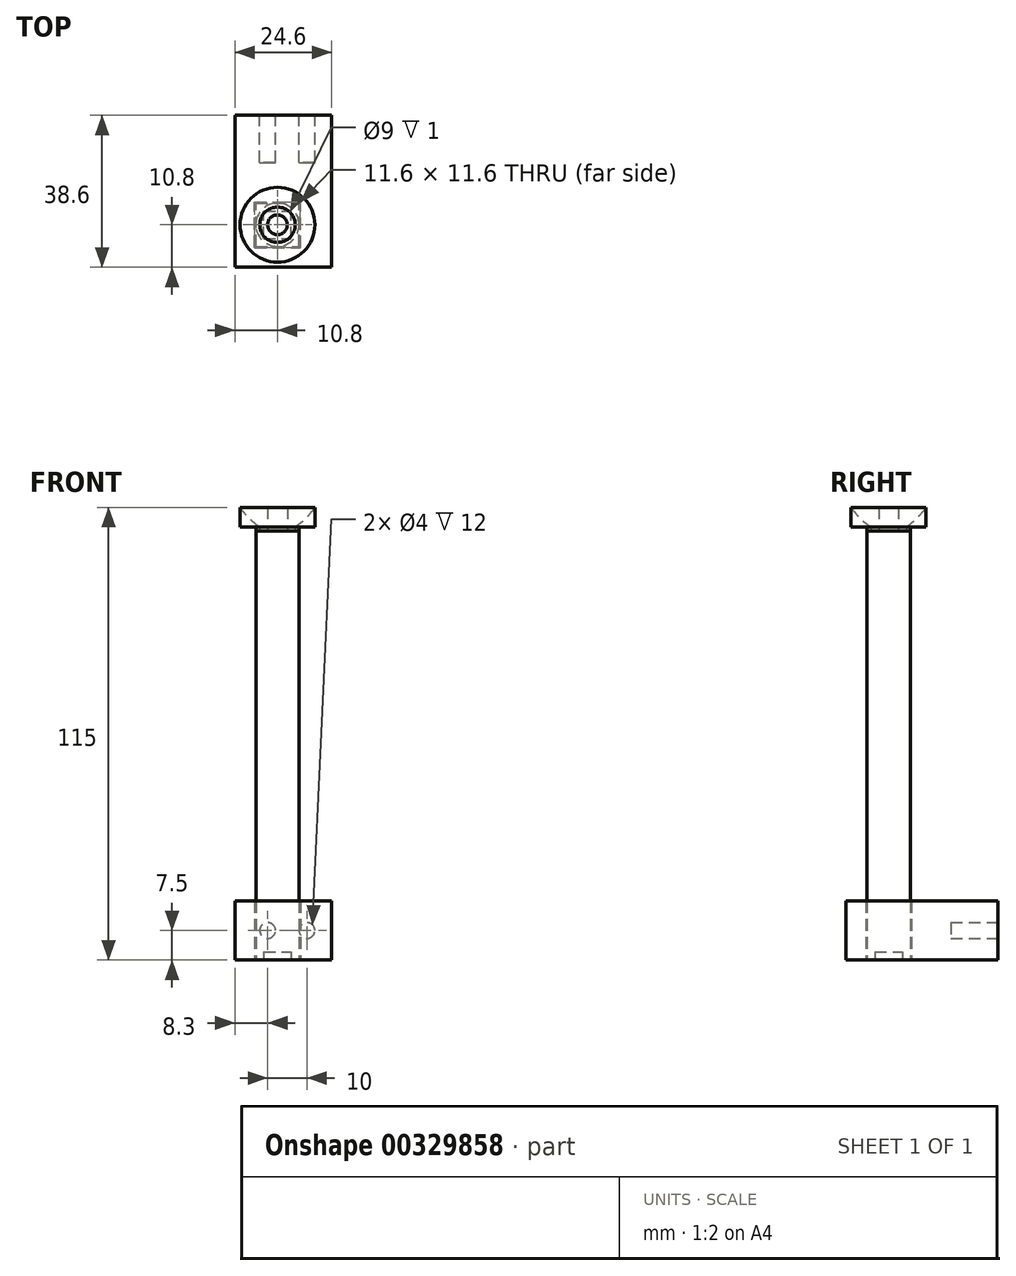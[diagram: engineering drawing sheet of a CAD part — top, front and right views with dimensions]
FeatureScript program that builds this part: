
annotation { "Feature Type Name" : "Feature", "Feature Type Description" : "" }
export const myFeature = defineFeature(function(context is Context, id is Id, definition is map)
    precondition{}
    {
        {
            var Q0;
            Q0=qCreatedBy(makeId("Top.planeOp"),FACE);
            var sketch = newSketch(context, id + "F0", { "sketchPlane" : qUnion([Q0])});
            skLineSegment(sketch, "E0.bottom", {"start": v(0, 0) * mm, "end": v(11, 0) * mm});
            skLineSegment(sketch, "E0.top", {"start": v(0, 11) * mm, "end": v(11, 11) * mm});
            skLineSegment(sketch, "E0.left", {"start": v(0, 0) * mm, "end": v(0, 11) * mm});
            skLineSegment(sketch, "E0.right", {"start": v(11, 0) * mm, "end": v(11, 11) * mm});
            skLineSegment(sketch, "E1.0", {"start": v(2, 2) * mm, "end": v(2, 9) * mm});
            skLineSegment(sketch, "E1.1", {"start": v(2, 2) * mm, "end": v(9, 2) * mm});
            skLineSegment(sketch, "E1.2", {"start": v(9, 2) * mm, "end": v(9, 9) * mm});
            skLineSegment(sketch, "E1.3", {"start": v(2, 9) * mm, "end": v(9, 9) * mm});
            skSolve(sketch);
        }
        {
            var Q0;
            Q0 = qSketchRegion(id + "F0", true);
            extrude(context, id + "F1", {"entities" : qUnion([Q0]), "depth" : 2 * mm, "offsetDistance" : 25 * mm});
        }
        {
            var Q0;
            Q0=makeQuery(id+"F1.opExtrude","CAP_FACE",FACE,{"disambiguationData":[OSD([sQuery(id+"F0.wireOp",EDGE,"E0.bottom"),sQuery(id+"F0.wireOp",EDGE,"E0.top"),sQuery(id+"F0.wireOp",EDGE,"E0.left"),sQuery(id+"F0.wireOp",EDGE,"E0.right"),sQuery(id+"F0.wireOp",EDGE,"E1.0"),sQuery(id+"F0.wireOp",EDGE,"E1.1"),sQuery(id+"F0.wireOp",EDGE,"E1.2"),sQuery(id+"F0.wireOp",EDGE,"E1.3")])],"isStart":false});
            var sketch = newSketch(context, id + "F2", { "sketchPlane" : qUnion([Q0])});
            skLineSegment(sketch, "E2.bottom", {"start": v(0, 0) * mm, "end": v(11, 0) * mm});
            skLineSegment(sketch, "E2.top", {"start": v(0, 11) * mm, "end": v(11, 11) * mm});
            skLineSegment(sketch, "E2.left", {"start": v(0, 0) * mm, "end": v(0, 11) * mm});
            skLineSegment(sketch, "E2.right", {"start": v(11, 0) * mm, "end": v(11, 11) * mm});
            skSolve(sketch);
        }
        {
            var Q0;
            Q0 = qSketchRegion(id + "F2", true);
            extrude(context, id + "F3", {"entities" : qUnion([Q0]), "operationType" : NewBodyOperationType.ADD, "depth" : 107 * mm, "offsetDistance" : 25 * mm});
        }
        {
            var Q0;
            Q0=makeQuery(id+"F3.opExtrude","CAP_FACE",FACE,{"disambiguationData":[OSD([sQuery(id+"F2.wireOp",EDGE,"E2.bottom"),sQuery(id+"F2.wireOp",EDGE,"E2.top"),sQuery(id+"F2.wireOp",EDGE,"E2.left"),sQuery(id+"F2.wireOp",EDGE,"E2.right")])],"isStart":false});
            var sketch = newSketch(context, id + "F4", { "sketchPlane" : qUnion([Q0])});
            skCircle(sketch, "E3", {"center": v(5.5, 5.5) * mm, "radius": 2.5 * mm});
            skPoint(sketch, "E3.centerSnap0", {"position": v(5.5, 11) * mm});
            skPoint(sketch, "E3.centerSnap1", {"position": v(0, 5.5) * mm});
            skSolve(sketch);
        }
        {
            var Q0;
            Q0=makeQuery(id+"F4.imprint","IMPRINT",FACE,{"disambiguationData":[TD([[makeQuery(id+"F4.imprint","IMPRINT",EDGE,{"derivedFrom":sQuery(id+"F4.wireOp",EDGE,"E3")}),1.0]])]});
            extrude(context, id + "F5", {"entities" : qUnion([Q0]), "operationType" : NewBodyOperationType.ADD, "depth" : 6 * mm, "offsetDistance" : 25 * mm});
        }
        {
            var Q0;
            Q0=makeQuery(id+"F3.opExtrude","CAP_FACE",FACE,{"disambiguationData":[OSD([sQuery(id+"F2.wireOp",EDGE,"E2.bottom"),sQuery(id+"F2.wireOp",EDGE,"E2.top"),sQuery(id+"F2.wireOp",EDGE,"E2.left"),sQuery(id+"F2.wireOp",EDGE,"E2.right")])],"isStart":false});
            cPlane(context, id + "F6", {"entities" : qUnion([Q0]), "cplaneType" : CPlaneType.OFFSET, "offset" : 1 * mm, "width" : 150 * mm, "height" : 150 * mm});
        }
        {
            var Q0;
            Q0=qCreatedBy(id+"F6.planeOp",FACE);
            var sketch = newSketch(context, id + "F7", { "sketchPlane" : qUnion([Q0])});
            skCircle(sketch, "E4.0", {"center": v(5.5, 5.5) * mm, "radius": 4.5 * mm});
            skCircle(sketch, "E5.0", {"center": v(5.5, 5.5) * mm, "radius": 9.5 * mm});
            skLineSegment(sketch, "E6", {"start": v(5.5, 5.5) * mm, "end": v(10, 5.5) * mm, "construction": true});
            skLineSegment(sketch, "E7", {"start": v(10, 5.5) * mm, "end": v(15, 5.5) * mm, "construction": true});
            skSolve(sketch);
        }
        {
            var Q0;
            Q0=makeQuery(id+"F3.boolean.opBoolean","MERGE",FACE,{"derivedFrom":[makeQuery(id+"F1.opExtrude","SWEPT_FACE",FACE,{"disambiguationData":[OSD([sQuery(id+"F0.wireOp",EDGE,"E0.bottom")])]}),makeQuery(id+"F3.opExtrude","SWEPT_FACE",FACE,{"disambiguationData":[OSD([sQuery(id+"F2.wireOp",EDGE,"E2.bottom")])]})]});
            var Q1;
            Q1=makeQuery(id+"F3.boolean.opBoolean","MERGE",FACE,{"derivedFrom":[makeQuery(id+"F1.opExtrude","SWEPT_FACE",FACE,{"disambiguationData":[OSD([sQuery(id+"F0.wireOp",EDGE,"E0.top")])]}),makeQuery(id+"F3.opExtrude","SWEPT_FACE",FACE,{"disambiguationData":[OSD([sQuery(id+"F2.wireOp",EDGE,"E2.top")])]})]});
            cPlane(context, id + "F8", {"entities" : qUnion([Q0, Q1]), "cplaneType" : CPlaneType.MID_PLANE, "offset" : 25 * mm, "width" : 150 * mm, "height" : 150 * mm});
        }
        {
            var Q0;
            Q0=qCreatedBy(id+"F8.planeOp",FACE);
            var sketch = newSketch(context, id + "F9", { "sketchPlane" : qUnion([Q0])});
            skLineSegment(sketch, "E8", {"start": v(15, 110) * mm, "end": v(15, 115) * mm});
            skLineSegment(sketch, "E9", {"start": v(15, 110) * mm, "end": v(10, 110) * mm});
            skArc(sketch, "E10", {"start": v(10, 110) * mm, "mid": v(12.75, 112.25) * mm, "end": v(15, 115) * mm});
            skLineSegment(sketch, "E11", {"start": v(10, 110) * mm, "end": v(10, 109) * mm});
            skLineSegment(sketch, "E12", {"start": v(10, 109) * mm, "end": v(11, 109) * mm});
            skLineSegment(sketch, "E13", {"start": v(11, 109) * mm, "end": v(11, 110) * mm});
            skSolve(sketch);
        }
        {
            var Q0;
            Q0 = qSketchRegion(id + "F9", true);
            var Q1;
            Q1=makeQuery(id+"F5.opExtrude","CAP_EDGE",EDGE,{"disambiguationData":[OSD([sQuery(id+"F4.wireOp",EDGE,"E3")])],"isStart":false});
            revolve(context, id + "F10", {"surfaceOperationType" : NewSurfaceOperationType.NEW, "entities" : qUnion([Q0]), "axis" : qUnion([Q1]), "revolveType" : RevolveType.FULL});
        }
        {
            var Q0;
            Q0=qCreatedBy(makeId("Top.planeOp"),FACE);
            var sketch = newSketch(context, id + "F11", { "sketchPlane" : qUnion([Q0])});
            skLineSegment(sketch, "E14.0", {"start": v(-0.3, -0.3) * mm, "end": v(11.3, -0.3) * mm});
            skLineSegment(sketch, "E14.1", {"start": v(-0.3, -0.3) * mm, "end": v(-0.3, 11.3) * mm});
            skLineSegment(sketch, "E14.2", {"start": v(-0.3, 11.3) * mm, "end": v(11.3, 11.3) * mm});
            skLineSegment(sketch, "E14.3", {"start": v(11.3, -0.3) * mm, "end": v(11.3, 11.3) * mm});
            skLineSegment(sketch, "E15.0", {"start": v(-5.3, -5.3) * mm, "end": v(-5.3, 33.3) * mm});
            skLineSegment(sketch, "E15.1", {"start": v(-5.3, -5.3) * mm, "end": v(19.3, -5.3) * mm});
            skLineSegment(sketch, "E15.2", {"start": v(19.3, -5.3) * mm, "end": v(19.3, 33.3) * mm});
            skLineSegment(sketch, "E16", {"start": v(-5.3, 33.3) * mm, "end": v(19.3, 33.3) * mm});
            skSolve(sketch);
        }
        {
            var Q0;
            Q0 = qSketchRegion(id + "F11", true);
            extrude(context, id + "F12", {"entities" : qUnion([Q0]), "depth" : 15 * mm, "offsetDistance" : 25 * mm});
        }
        {
            var Q0;
            Q0=makeQuery(id+"F12.opExtrude","SWEPT_FACE",FACE,{"disambiguationData":[OSD([sQuery(id+"F11.wireOp",EDGE,"E16")])]});
            var sketch = newSketch(context, id + "F13", { "sketchPlane" : qUnion([Q0])});
            skLineSegment(sketch, "E17", {"start": v(-19.3, 7.5) * mm, "end": v(-13, 7.5) * mm, "construction": true});
            skCircle(sketch, "E18", {"center": v(-13, 7.5) * mm, "radius": 2 * mm});
            skCircle(sketch, "E19", {"center": v(-3, 7.5) * mm, "radius": 2 * mm});
            skSolve(sketch);
        }
        {
            var Q0;
            Q0 = qSketchRegion(id + "F13", true);
            extrude(context, id + "F14", {"entities" : qUnion([Q0]), "operationType" : NewBodyOperationType.REMOVE, "oppositeDirection" : true, "depth" : 12 * mm, "offsetDistance" : 25 * mm});
        }
    });
